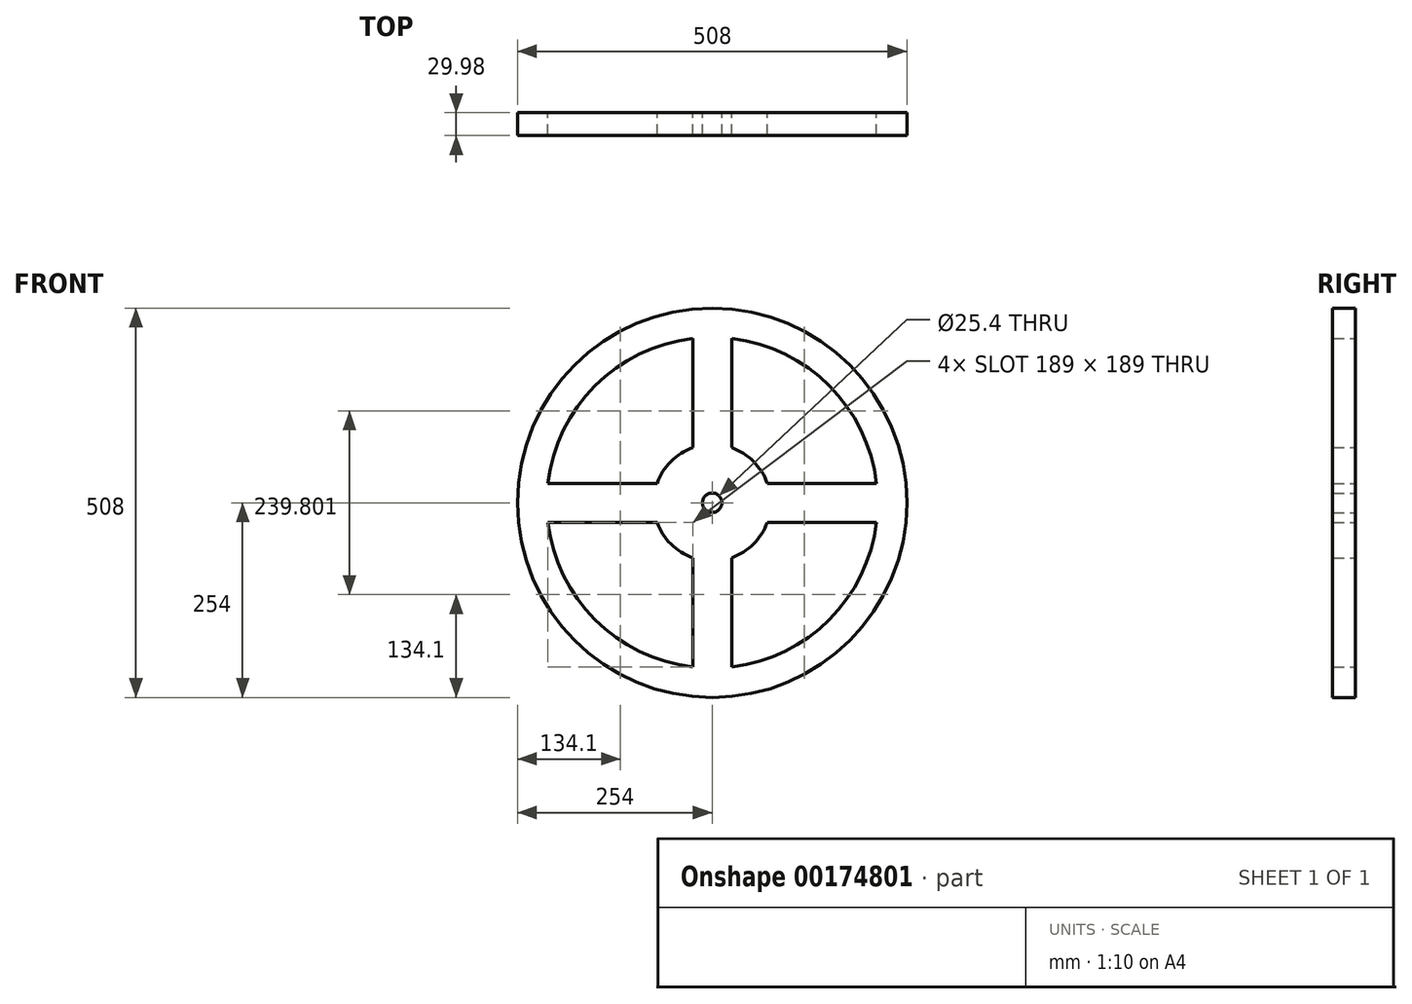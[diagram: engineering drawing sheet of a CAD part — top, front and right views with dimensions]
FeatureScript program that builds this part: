
annotation { "Feature Type Name" : "Feature", "Feature Type Description" : "" }
export const myFeature = defineFeature(function(context is Context, id is Id, definition is map)
    precondition{}
    {
        {
            var Q0;
            Q0=qCreatedBy(makeId("Front.planeOp"),FACE);
            var sketch = newSketch(context, id + "F0", { "sketchPlane" : qUnion([Q0])});
            skCircle(sketch, "E0", {"center": v(0, 0) * mm, "radius": 254 * mm});
            skArc(sketch, "E1", {"start": v(-214.4, -25.4) * mm, "mid": v(-152.66, -152.66) * mm, "end": v(-25.4, -214.4) * mm});
            skCircle(sketch, "E2", {"center": v(0, 0) * mm, "radius": 12.7 * mm});
            skLineSegment(sketch, "E3", {"start": v(0, 0) * mm, "end": v(0, 215.9) * mm, "construction": true});
            skLineSegment(sketch, "E4", {"start": v(0, 0) * mm, "end": v(-215.9, 0) * mm, "construction": true});
            skLineSegment(sketch, "E5", {"start": v(0, 0) * mm, "end": v(215.9, 0) * mm, "construction": true});
            skLineSegment(sketch, "E6", {"start": v(0, 0) * mm, "end": v(0, -215.9) * mm, "construction": true});
            skLineSegment(sketch, "E7.0", {"start": v(25.4, 71.84) * mm, "end": v(25.4, 214.4) * mm});
            skLineSegment(sketch, "E8.0", {"start": v(-25.4, 71.84) * mm, "end": v(-25.4, 214.4) * mm});
            skLineSegment(sketch, "E9.0", {"start": v(-71.84, -25.4) * mm, "end": v(-214.4, -25.4) * mm});
            skLineSegment(sketch, "E10.0", {"start": v(-71.84, 25.4) * mm, "end": v(-214.4, 25.4) * mm});
            skLineSegment(sketch, "E11.0", {"start": v(71.84, 25.4) * mm, "end": v(214.4, 25.4) * mm});
            skLineSegment(sketch, "E12.0", {"start": v(71.84, -25.4) * mm, "end": v(214.4, -25.4) * mm});
            skLineSegment(sketch, "E13.0", {"start": v(25.4, -71.84) * mm, "end": v(25.4, -214.4) * mm});
            skLineSegment(sketch, "E14.0", {"start": v(-25.4, -71.84) * mm, "end": v(-25.4, -214.4) * mm});
            skLineSegment(sketch, "E15.trimOffspring", {"start": v(-252.73, 25.4) * mm, "end": v(-254, 25.4) * mm});
            skLineSegment(sketch, "E16.trimOffspring", {"start": v(-252.73, -25.4) * mm, "end": v(-254, -25.4) * mm});
            skLineSegment(sketch, "E17.trimOffspring", {"start": v(-25.4, 252.73) * mm, "end": v(-25.4, 254) * mm});
            skLineSegment(sketch, "E18.trimOffspring", {"start": v(25.4, 252.73) * mm, "end": v(25.4, 254) * mm});
            skLineSegment(sketch, "E19.trimOffspring", {"start": v(252.73, 25.4) * mm, "end": v(254, 25.4) * mm});
            skLineSegment(sketch, "E20.trimOffspring", {"start": v(252.73, -25.4) * mm, "end": v(254, -25.4) * mm});
            skLineSegment(sketch, "E21.trimOffspring", {"start": v(25.4, -252.73) * mm, "end": v(25.4, -254) * mm});
            skLineSegment(sketch, "E22.trimOffspring", {"start": v(-25.4, -252.73) * mm, "end": v(-25.4, -254) * mm});
            skArc(sketch, "E23.trimOffspring", {"start": v(-25.4, 214.4) * mm, "mid": v(-152.66, 152.66) * mm, "end": v(-214.4, 25.4) * mm});
            skArc(sketch, "E24.trimOffspring", {"start": v(214.4, 25.4) * mm, "mid": v(152.66, 152.66) * mm, "end": v(25.4, 214.4) * mm});
            skArc(sketch, "E25.trimOffspring", {"start": v(25.4, -214.4) * mm, "mid": v(152.66, -152.66) * mm, "end": v(214.4, -25.4) * mm});
            skArc(sketch, "E26", {"start": v(-76.2, 0) * mm, "mid": v(-62.22, -44) * mm, "end": v(-25.4, -71.84) * mm});
            skArc(sketch, "E27.trimOffspring", {"start": v(-25.4, 71.84) * mm, "mid": v(-53.88, 53.88) * mm, "end": v(-71.84, 25.4) * mm});
            skArc(sketch, "E28.trimOffspring", {"start": v(71.84, 25.4) * mm, "mid": v(53.88, 53.88) * mm, "end": v(25.4, 71.84) * mm});
            skArc(sketch, "E29.trimOffspring", {"start": v(25.4, -71.84) * mm, "mid": v(53.88, -53.88) * mm, "end": v(71.84, -25.4) * mm});
            skSolve(sketch);
        }
        {
            var Q0;
            Q0 = qSketchRegion(id + "F0", true);
            var Q1;
            {var subQ5=sQuery(id+"F0.wireOp",EDGE,"E27.trimOffspring");Q1=makeQuery(id+"F0.imprint","IMPRINT",FACE,{"disambiguationData":[TD([[makeQuery(id+"F0.imprint","IMPRINT",EDGE,{"derivedFrom":subQ5}),1.0]])]});}
            var Q2;
            {var subQ5=sQuery(id+"F0.wireOp",EDGE,"E28.trimOffspring");Q2=makeQuery(id+"F0.imprint","IMPRINT",FACE,{"disambiguationData":[TD([[makeQuery(id+"F0.imprint","IMPRINT",EDGE,{"derivedFrom":subQ5}),1.0]])]});}
            var Q3;
            {var subQ5=sQuery(id+"F0.wireOp",EDGE,"E29.trimOffspring");Q3=makeQuery(id+"F0.imprint","IMPRINT",FACE,{"disambiguationData":[TD([[makeQuery(id+"F0.imprint","IMPRINT",EDGE,{"derivedFrom":subQ5}),1.0]])]});}
            var Q4;
            {var subQ0=sQuery(id+"F0.wireOp",EDGE,"E9.0");var subQ1=sQuery(id+"F0.wireOp",EDGE,"E2");var subQ2=makeQuery(id+"F0.imprint","INTERSECT",VERTEX,{"derivedFrom":[subQ1,subQ0]});Q4=makeQuery(id+"F0.imprint","IMPRINT",FACE,{"disambiguationData":[TD([[makeQuery(id+"F0.imprint","IMPRINT",EDGE,{"disambiguationData":[TD([[subQ2,-1.0]])],"derivedFrom":subQ1}),-1.0]])]});}
            extrude(context, id + "F1", {"entities" : qUnion([Q0, Q1, Q2, Q3, Q4]), "endBound" : BoundingType.SYMMETRIC, "depth" : 29.97 * mm});
        }
    });
